# Revit family: z_PlumFixt_ZIP_Micro
name_source: partatom
category: Plumbing Fixtures
revit_build: Autodesk Revit 2016 (Build: 20150220_1215(x64)
units: mm (PartAtom-declared; Revit-internal decimal feet)

## family parameters
Always vertical = No
Cut with Voids When Loaded = Yes
OmniClass Number = 23.45.55.17
OmniClass Title = Mixing Faucets
Part Type = Normal
Room Calculation Point = No
Round Connector Dimension = Use Diameter
Shared = No
Work Plane-Based = Yes

## types (2) — shared parameters
CW Connection = Yes
HW Connection = Yes
Manufacturer = Zip Australia
Manufacturer_Overall Depth = 135 mm  [stored 0.442913 ft]
Manufacturer_Overall Height = 320 mm
Manufacturer_Overall Width = 46 mm  [stored 0.150919 ft]
ModifiedIssue_ANZRS = 20190702 $
URL = https://www.zipwater.com
Vent Connection = No
Waste Connection = No
zero-valued in all types: Default Elevation

## per-type parameters (varying)
| type | Fixture Material | Manufacturer_Spec Code | Model |
| Bright Chrome | z_ZIP Micro_Metal_Bright Chrome | Z0 | Z0 - Bright Chrome |
| Matte Black | z_ZIP Micro_Metal_Matte Black | Z3 | Z3 - Matte Black |

note: [stored X ft] marks values corroborated as IEEE doubles in the binary element streams (Revit-internal decimal feet)

## geometry (parser evidence)
native form markers: Sweep x3
no freeform markers — native parametric forms only
